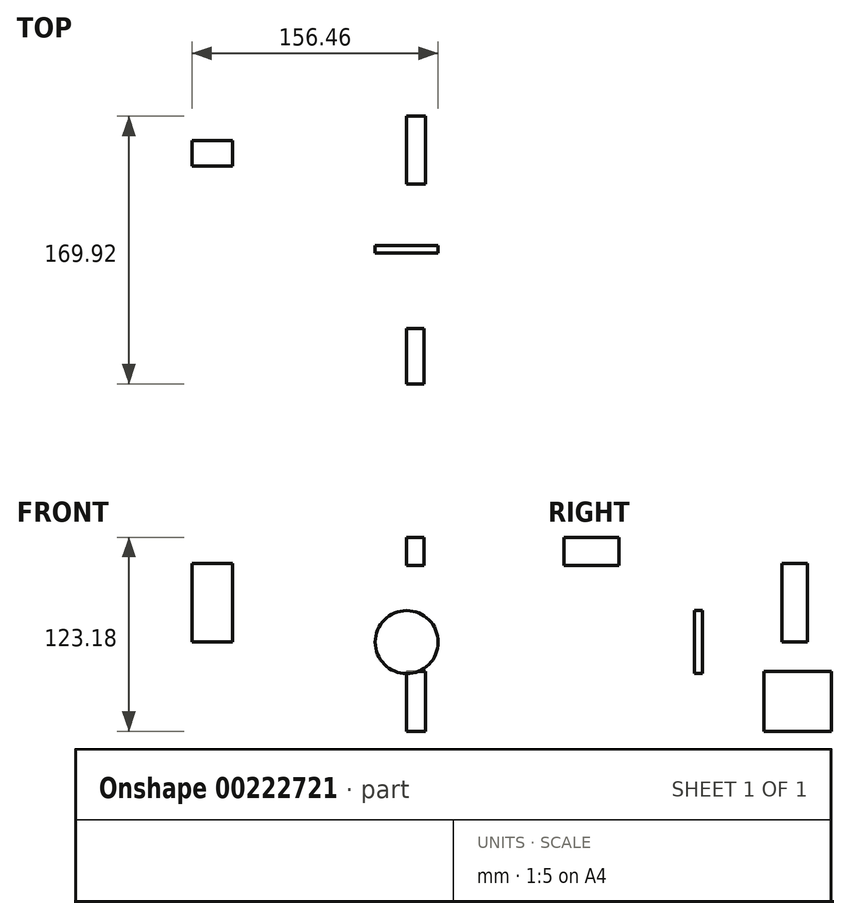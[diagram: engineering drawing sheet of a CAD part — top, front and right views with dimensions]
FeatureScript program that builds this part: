
annotation { "Feature Type Name" : "Feature", "Feature Type Description" : "" }
export const myFeature = defineFeature(function(context is Context, id is Id, definition is map)
    precondition{}
    {
        {
            var Q0;
            Q0=qCreatedBy(makeId("Top.planeOp"),FACE);
            var sketch = newSketch(context, id + "F0", { "sketchPlane" : qUnion([Q0])});
            skLineSegment(sketch, "E0.bottom", {"start": v(-136.46, 66.5) * mm, "end": v(-110.46, 66.5) * mm});
            skLineSegment(sketch, "E0.top", {"start": v(-136.46, 50.5) * mm, "end": v(-110.46, 50.5) * mm});
            skLineSegment(sketch, "E0.left", {"start": v(-136.46, 66.5) * mm, "end": v(-136.46, 50.5) * mm});
            skLineSegment(sketch, "E0.right", {"start": v(-110.46, 66.5) * mm, "end": v(-110.46, 50.5) * mm});
            skSolve(sketch);
        }
        {
            var Q0;
            Q0=makeQuery(id+"F0.imprint","IMPRINT",FACE,{"disambiguationData":[TD([[makeQuery(id+"F0.imprint","IMPRINT",EDGE,{"derivedFrom":sQuery(id+"F0.wireOp",EDGE,"E0.bottom")}),-1.0]])]});
            extrude(context, id + "F1", {"entities" : qUnion([Q0]), "depth" : 50 * mm, "offsetDistance" : 25 * mm});
        }
        {
            var Q0;
            Q0=qCreatedBy(makeId("Front.planeOp"),FACE);
            var sketch = newSketch(context, id + "F2", { "sketchPlane" : qUnion([Q0])});
            skCircle(sketch, "E1", {"center": v(0, 0) * mm, "radius": 20 * mm});
            skSolve(sketch);
        }
        {
            var Q0;
            Q0=makeQuery(id+"F2.imprint","IMPRINT",FACE,{"disambiguationData":[TD([[makeQuery(id+"F2.imprint","IMPRINT",EDGE,{"derivedFrom":sQuery(id+"F2.wireOp",EDGE,"E1")}),1.0]])]});
            extrude(context, id + "F3", {"entities" : qUnion([Q0]), "depth" : 5 * mm, "offsetDistance" : 25 * mm});
        }
        {
            var Q0;
            Q0=qCreatedBy(makeId("Right.planeOp"),FACE);
            var sketch = newSketch(context, id + "F4", { "sketchPlane" : qUnion([Q0])});
            skLineSegment(sketch, "E2.bottom", {"start": v(39, -18.58) * mm, "end": v(82, -18.58) * mm});
            skLineSegment(sketch, "E2.top", {"start": v(39, -56.58) * mm, "end": v(82, -56.58) * mm});
            skLineSegment(sketch, "E2.left", {"start": v(39, -18.58) * mm, "end": v(39, -56.58) * mm});
            skLineSegment(sketch, "E2.right", {"start": v(82, -18.58) * mm, "end": v(82, -56.58) * mm});
            skSolve(sketch);
        }
        {
            var Q0;
            Q0=makeQuery(id+"F4.imprint","IMPRINT",FACE,{"disambiguationData":[TD([[makeQuery(id+"F4.imprint","IMPRINT",EDGE,{"derivedFrom":sQuery(id+"F4.wireOp",EDGE,"E2.bottom")}),-1.0]])]});
            extrude(context, id + "F5", {"entities" : qUnion([Q0]), "depth" : 12 * mm, "offsetDistance" : 25 * mm});
        }
        {
            var Q0;
            Q0=qCreatedBy(makeId("Right.planeOp"),FACE);
            var sketch = newSketch(context, id + "F6", { "sketchPlane" : qUnion([Q0])});
            skLineSegment(sketch, "E3.bottom", {"start": v(-87.92, 66.6) * mm, "end": v(-52.92, 66.6) * mm});
            skLineSegment(sketch, "E3.top", {"start": v(-87.92, 48.6) * mm, "end": v(-52.92, 48.6) * mm});
            skLineSegment(sketch, "E3.left", {"start": v(-87.92, 66.6) * mm, "end": v(-87.92, 48.6) * mm});
            skLineSegment(sketch, "E3.right", {"start": v(-52.92, 66.6) * mm, "end": v(-52.92, 48.6) * mm});
            skSolve(sketch);
        }
        {
            var Q0;
            Q0=makeQuery(id+"F6.imprint","IMPRINT",FACE,{"disambiguationData":[TD([[makeQuery(id+"F6.imprint","IMPRINT",EDGE,{"derivedFrom":sQuery(id+"F6.wireOp",EDGE,"E3.bottom")}),-1.0]])]});
            extrude(context, id + "F7", {"entities" : qUnion([Q0]), "depth" : 11 * mm, "offsetDistance" : 25 * mm});
        }
    });
